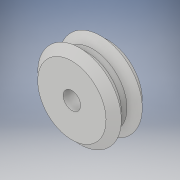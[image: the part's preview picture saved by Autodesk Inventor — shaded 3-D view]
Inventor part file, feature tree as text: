
AUTODESK INVENTOR PART (.ipt)
format: ipt  version: 2019 (Build 230136000, 136)  size: 119,296 bytes
history: native  units: in
note: dims shown in document units (in); Inventor stores cm internally (conversion verified against a paired STEP export)
features: revolve x1, sketch x1
ambient origin geometry x8: Origin, YZ Plane, XZ Plane, XY Plane, X Axis, Y Axis, Z Axis, Center Point
bodies: Solid1 (feature_tree)
feature tree (2):
  revolve  "Revolution1"  [1 undecoded]
  sketch  "Sketch1"  dims[d0=0.0984in d1=0.4724in d2=0.2366in d3=45.0deg d4=0.0in d5=0.4094in d6=90.0deg]
note: 1 required parameter value undecoded (feature->parameter linkage not recoverable at this tier; creation-order binding heuristic only, values carry confidence <= 0.55)
